# Revit family: Shower-Wall_Supply_Holder-KOHLER-BEITOU-K-99861T
name_source: partatom
category: Plumbing Fixtures
revit_build: Autodesk Revit 2017 (Build: 20160225_1515(x64)
units: mm (PartAtom-declared; Revit-internal decimal feet)

## family parameters
Cut with Voids When Loaded = No
Host = Face
OmniClass Number = 23.31.17.00
OmniClass Title = Showers
Part Type = Normal
Room Calculation Point = No
Round Connector Dimension = Use Diameter
Shared = No

## types (1)
- CP-Polished Chrome
    ADA Compliant = No
    Assembly Code = C1030200
    CW Connection = No
    Cold Water Inlet = Cold Water Inlet
    Date Modified = 09/28/2020
    Default Elevation = 42"
    Description = Manda shower bracket (water can enter)
    Drain Included = No
    Finish = Kohler-Metal-CP-Polished_Chrome
    HW Connection = Yes
    Height = 2 1/4"
    Hot Water Inlet = Hot Water Inlet
    Length = 4 1/8"
    Manufacturer = KOHLER Co.
    Master Format 2014 = 10 28 00
    Master Format 2014 Name = Toilet, Bath, and Laundry Accessories
    Material = Premium Metal Construction
    Model = K-99861T-CP
    Product Documentation Link = https://files.kohler.com.cn
    Product Name = BEITOU
    Product Page URL = https://www.kohler.com.cn
    Tempered Water Inlet = Tempered Water Inlet
    Type = 1
    URL = https://www.kohler.com.cn
    Vent Connection = No
    Waste Connection = No
    Waste Water Outlet = Waste Water Outlet
    WaterSense Certified = No
    Width = 8 7/16"

## geometry (parser evidence)
native form markers: Sweep x4
no freeform markers — native parametric forms only
